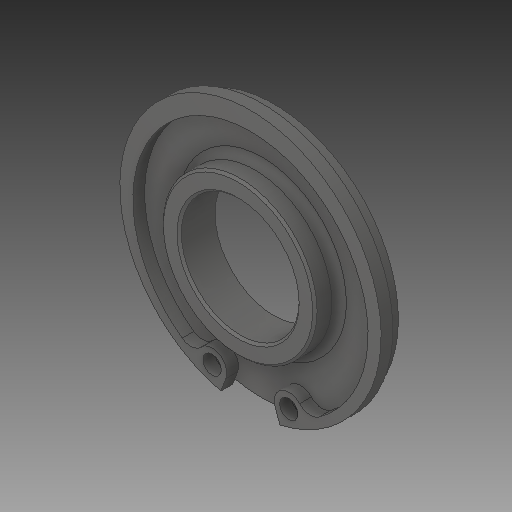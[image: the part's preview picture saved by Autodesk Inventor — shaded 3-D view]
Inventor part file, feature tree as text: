
AUTODESK INVENTOR PART (.ipt)
format: ipt  version: 2018 (Build 220112000, 112)  size: 171,008 bytes
history: native  units: in
note: dims shown in document units (in); Inventor stores cm internally (conversion verified against a paired STEP export)
features: chamfer x1
ambient origin geometry x8: Origin, YZ Plane, XZ Plane, XY Plane, X Axis, Y Axis, Z Axis, Center Point
bodies: Solid1 (feature_tree)
feature tree (1):
  chamfer  "Chamfer1"  [1 undecoded]
note: 1 required parameter value undecoded (feature->parameter linkage not recoverable at this tier; creation-order binding heuristic only, values carry confidence <= 0.55)
